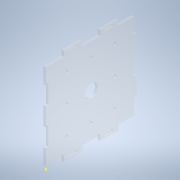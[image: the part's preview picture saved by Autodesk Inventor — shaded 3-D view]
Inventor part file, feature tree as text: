
AUTODESK INVENTOR PART (.ipt)
format: ipt  version: 2020 (Build 240168000, 168)  size: 200,192 bytes
history: native  units: mm
features: sketch x11, hole x9, extrude x1
ambient origin geometry x8: Origin, YZ Plane, XZ Plane, XY Plane, X Axis, Y Axis, Z Axis, Center Point
bodies: Solid1 (feature_tree)
feature tree (21):
  extrude  "Extrusion1"  Depth=10.0mm
  hole  "Hole1"  [1 undecoded]
  hole  "Hole4"  [1 undecoded]
  sketch  "Sketch6"  dims[d54=3.0mm d55=6.0mm d56=4.0mm d57=2.0mm d58=90.0deg d59=8.0mm d60=20.594885mm d61=3.0mm]
  sketch  "Sketch7"  dims[d62=3.0mm d63=6.0mm d64=4.0mm d65=2.0mm d66=90.0deg d67=8.0mm d68=20.594885mm d69=3.0mm]
  hole  "Hole5"  [1 undecoded]
  hole  "Hole6"  [1 undecoded]
  hole  "Hole7"  [1 undecoded]
  hole  "Hole8"  [1 undecoded]
  hole  "Hole9"  [1 undecoded]
  hole  "Hole10"  [1 undecoded]
  hole  "Hole11"  [1 undecoded]
  sketch  "Sketch1"  dims[d4=3.0mm d5=0.0mm d6=10.0mm]
  sketch  "Sketch3"  dims[d7=15.0mm d8=6.0mm d9=4.0mm d10=2.0mm d11=90.0deg d12=8.0mm d13=20.594885mm d45=3.0mm]
  sketch  "Sketch5"  dims[d46=3.0mm d47=6.0mm d48=4.0mm d49=2.0mm d50=90.0deg d51=8.0mm d52=20.594885mm d53=3.0mm]
  sketch  "Sketch8"  dims[d70=3.0mm d71=6.0mm d72=4.0mm d73=2.0mm d74=90.0deg d75=8.0mm d76=20.594885mm d77=3.0mm]
  sketch  "Sketch9"  dims[d78=3.0mm d79=6.0mm d80=4.0mm d81=2.0mm d82=90.0deg d83=8.0mm d84=20.594885mm d85=3.0mm]
  sketch  "Sketch10"  dims[d86=3.0mm d87=6.0mm d88=4.0mm d89=2.0mm d90=90.0deg d91=8.0mm d92=20.594885mm d93=3.0mm]
  sketch  "Sketch11"  dims[d94=3.0mm d95=6.0mm d96=4.0mm d97=2.0mm d98=90.0deg d99=8.0mm d100=20.594885mm d101=3.0mm]
  sketch  "Sketch12"  dims[d102=3.0mm d103=6.0mm d104=4.0mm d105=2.0mm d106=90.0deg d107=8.0mm d108=20.594885mm d109=10.0mm]
  sketch  "Sketch13"  dims[d110=10.0mm d111=1.0mm d112=10.0mm d113=1.0mm d114=10.0mm d20=1.0mm d21=1.0mm d22=1.0mm d23=0.15mm d24=0.25mm d25=0.375mm d26=14.3117mm d27=0.75mm d28=20.594885mm d29=0.0625mm d30=0.75mm d31=0.375mm]
note: 9 required parameter values undecoded (feature->parameter linkage not recoverable at this tier; creation-order binding heuristic only, values carry confidence <= 0.55)
